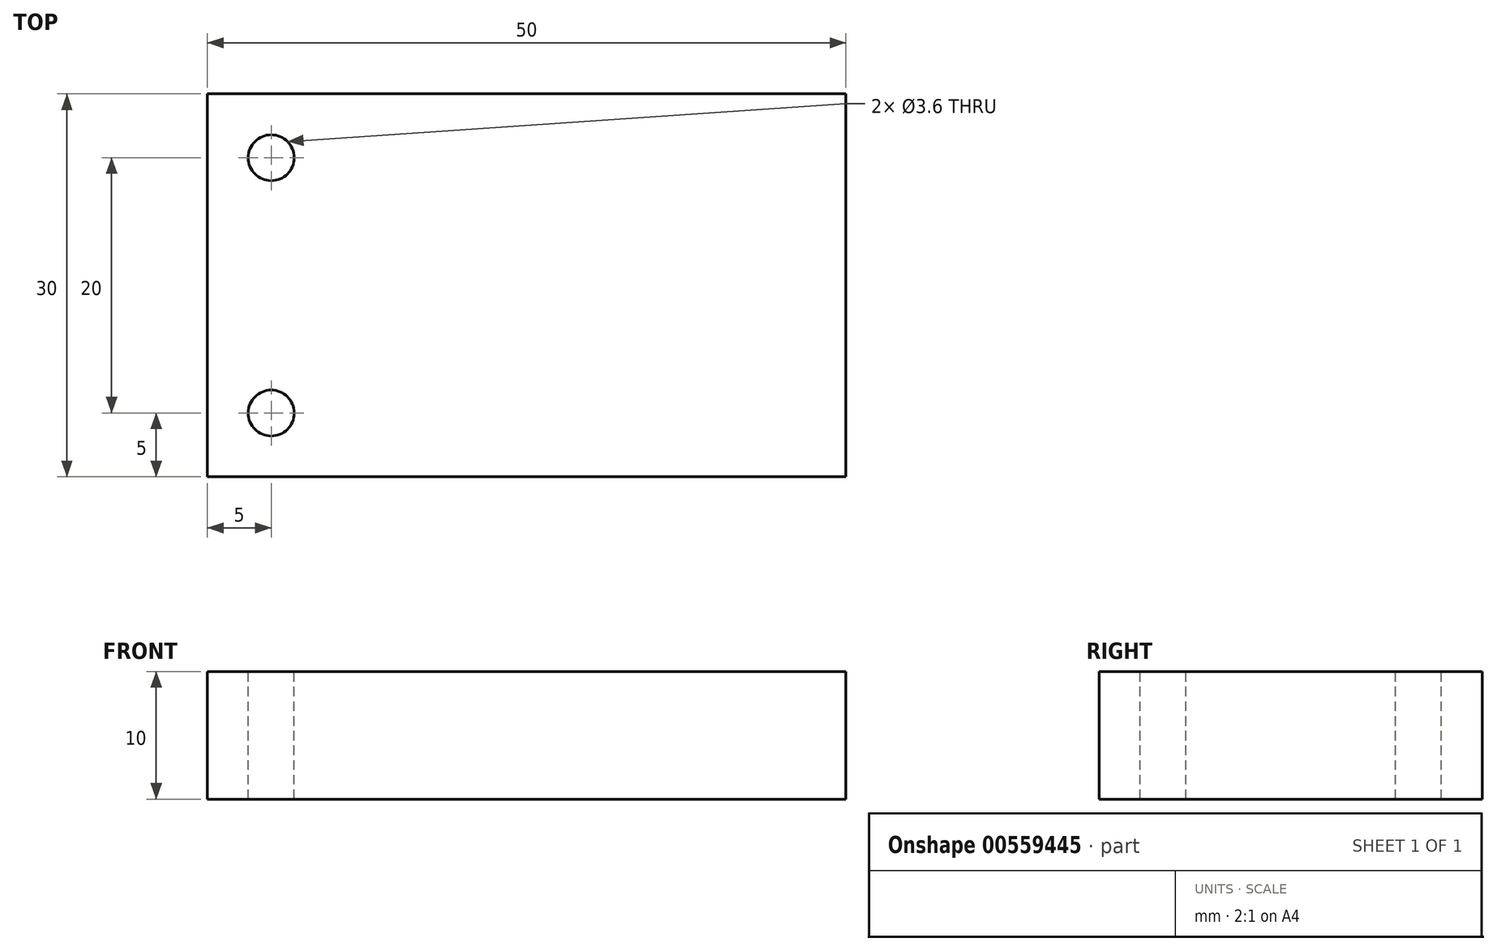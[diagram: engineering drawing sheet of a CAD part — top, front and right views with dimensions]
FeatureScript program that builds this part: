
annotation { "Feature Type Name" : "Feature", "Feature Type Description" : "" }
export const myFeature = defineFeature(function(context is Context, id is Id, definition is map)
    precondition{}
    {
        {
            var Q0;
            Q0=qCreatedBy(makeId("Top.planeOp"),FACE);
            var sketch = newSketch(context, id + "F0", { "sketchPlane" : qUnion([Q0])});
            skLineSegment(sketch, "E0.bottom", {"start": v(25, 15) * mm, "end": v(-25, 15) * mm});
            skLineSegment(sketch, "E0.top", {"start": v(25, -15) * mm, "end": v(-25, -15) * mm});
            skLineSegment(sketch, "E0.left", {"start": v(25, 15) * mm, "end": v(25, -15) * mm});
            skLineSegment(sketch, "E0.right", {"start": v(-25, 15) * mm, "end": v(-25, -15) * mm});
            skPoint(sketch, "E0.middle", {"position": v(0, 0) * mm});
            skSolve(sketch);
        }
        {
            var Q0;
            Q0=qSketchRegion(id+"F0",true);
            extrude(context, id + "F1", {"entities" : qUnion([Q0]), "depth" : 10 * mm, "offsetDistance" : 25 * mm});
        }
        {
            var Q0;
            Q0=makeQuery(id+"F1.opExtrude","CAP_FACE",FACE,{"disambiguationData":[OSD([sQuery(id+"F0.wireOp",EDGE,"E0.bottom"),sQuery(id+"F0.wireOp",EDGE,"E0.top"),sQuery(id+"F0.wireOp",EDGE,"E0.left"),sQuery(id+"F0.wireOp",EDGE,"E0.right")])],"isStart":false});
            var sketch = newSketch(context, id + "F2", { "sketchPlane" : qUnion([Q0])});
            skCircle(sketch, "E1", {"center": v(-20, 10) * mm, "radius": 1.8 * mm});
            skCircle(sketch, "E2", {"center": v(-20, -10) * mm, "radius": 1.8 * mm});
            skSolve(sketch);
        }
        {
            var Q0;
            Q0=qSketchRegion(id+"F2",true);
            extrude(context, id + "F3", {"entities" : qUnion([Q0]), "operationType" : NewBodyOperationType.REMOVE, "oppositeDirection" : true, "depth" : 15 * mm, "offsetDistance" : 25 * mm});
        }
    });
